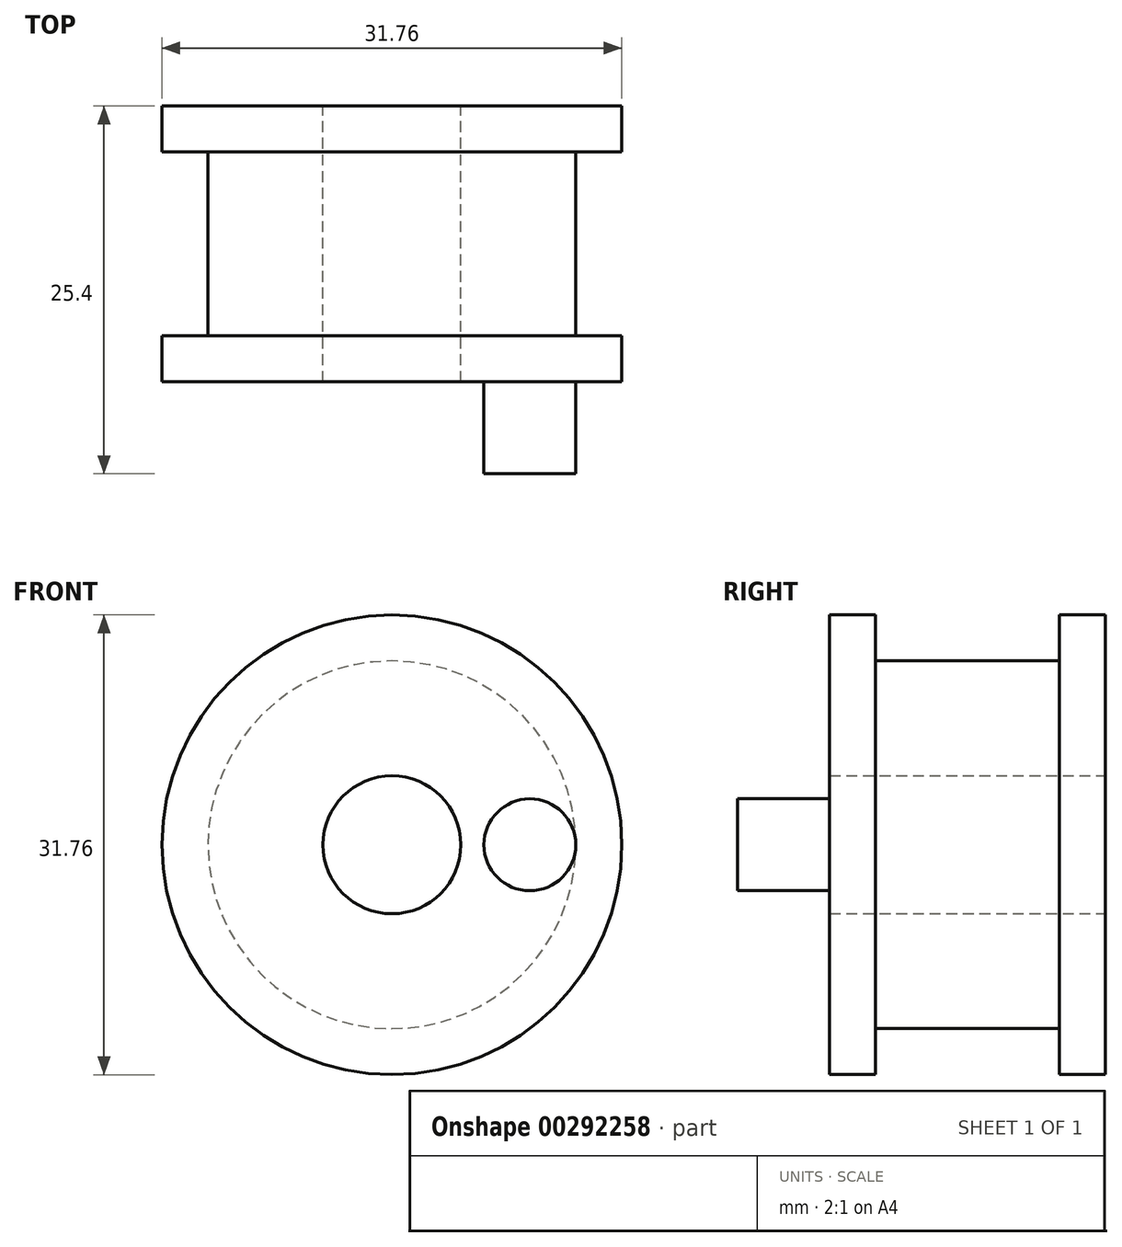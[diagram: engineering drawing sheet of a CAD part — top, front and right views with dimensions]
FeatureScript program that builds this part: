
annotation { "Feature Type Name" : "Feature", "Feature Type Description" : "" }
export const myFeature = defineFeature(function(context is Context, id is Id, definition is map)
    precondition{}
    {
        {
            var Q0;
            Q0=qCreatedBy(makeId("Front.planeOp"),FACE);
            var sketch = newSketch(context, id + "F0", { "sketchPlane" : qUnion([Q0])});
            skCircle(sketch, "E0", {"center": v(0, 0) * mm, "radius": 15.88 * mm});
            skCircle(sketch, "E1", {"center": v(0, 0) * mm, "radius": 4.76 * mm});
            skSolve(sketch);
        }
        {
            var Q0;
            Q0=makeQuery(id+"F0.imprint","IMPRINT",FACE,{"disambiguationData":[TD([[makeQuery(id+"F0.imprint","IMPRINT",EDGE,{"derivedFrom":sQuery(id+"F0.wireOp",EDGE,"E0")}),1.0]])]});
            extrude(context, id + "F1", {"entities" : qUnion([Q0]), "depth" : 3.17 * mm});
        }
        {
            var Q0;
            Q0=makeQuery(id+"F1.opExtrude","CAP_FACE",FACE,{"disambiguationData":[OSD([sQuery(id+"F0.wireOp",EDGE,"E0"),sQuery(id+"F0.wireOp",EDGE,"E1")])],"isStart":false});
            var sketch = newSketch(context, id + "F2", { "sketchPlane" : qUnion([Q0])});
            skCircle(sketch, "E2", {"center": v(0, 0) * mm, "radius": 12.7 * mm});
            skCircle(sketch, "E3", {"center": v(0, 0) * mm, "radius": 4.76 * mm});
            skSolve(sketch);
        }
        {
            var Q0;
            Q0=makeQuery(id+"F2.imprint","IMPRINT",FACE,{"disambiguationData":[TD([[makeQuery(id+"F2.imprint","IMPRINT",EDGE,{"derivedFrom":sQuery(id+"F2.wireOp",EDGE,"E2")}),1.0]])]});
            extrude(context, id + "F3", {"entities" : qUnion([Q0]), "operationType" : NewBodyOperationType.ADD, "depth" : 12.7 * mm});
        }
        {
            var Q0;
            Q0=makeQuery(id+"F3.opExtrude","CAP_FACE",FACE,{"disambiguationData":[OSD([sQuery(id+"F2.wireOp",EDGE,"E2"),sQuery(id+"F2.wireOp",EDGE,"E3")])],"isStart":false});
            var sketch = newSketch(context, id + "F4", { "sketchPlane" : qUnion([Q0])});
            skCircle(sketch, "E4", {"center": v(0, 0) * mm, "radius": 15.88 * mm});
            skCircle(sketch, "E5", {"center": v(0, 0) * mm, "radius": 4.76 * mm});
            skSolve(sketch);
        }
        {
            var Q0;
            Q0=makeQuery(id+"F4.imprint","IMPRINT",FACE,{"disambiguationData":[TD([[makeQuery(id+"F4.imprint","IMPRINT",EDGE,{"derivedFrom":sQuery(id+"F4.wireOp",EDGE,"E5")}),-1.0]])]});
            var Q1;
            Q1=makeQuery(id+"F4.imprint","IMPRINT",FACE,{"disambiguationData":[TD([[makeQuery(id+"F4.imprint","IMPRINT",EDGE,{"derivedFrom":sQuery(id+"F4.wireOp",EDGE,"E4")}),1.0]])]});
            extrude(context, id + "F5", {"entities" : qUnion([Q0, Q1]), "operationType" : NewBodyOperationType.ADD, "depth" : 3.17 * mm});
        }
        {
            var Q0;
            Q0=makeQuery(id+"F5.opExtrude","CAP_FACE",FACE,{"disambiguationData":[OSD([sQuery(id+"F4.wireOp",EDGE,"E4"),sQuery(id+"F4.wireOp",EDGE,"E5")])],"isStart":false});
            var sketch = newSketch(context, id + "F6", { "sketchPlane" : qUnion([Q0])});
            skLineSegment(sketch, "E6", {"start": v(0, 0) * mm, "end": v(9.53, 0) * mm});
            skCircle(sketch, "E7", {"center": v(9.53, 0) * mm, "radius": 3.18 * mm});
            skSolve(sketch);
        }
        {
            var Q0;
            Q0=makeQuery(id+"F6.imprint","IMPRINT",FACE,{"disambiguationData":[TD([[makeQuery(id+"F6.imprint","IMPRINT",EDGE,{"derivedFrom":sQuery(id+"F6.wireOp",EDGE,"E7")}),1.0]])]});
            extrude(context, id + "F7", {"entities" : qUnion([Q0]), "operationType" : NewBodyOperationType.ADD, "depth" : 6.35 * mm});
        }
    });
